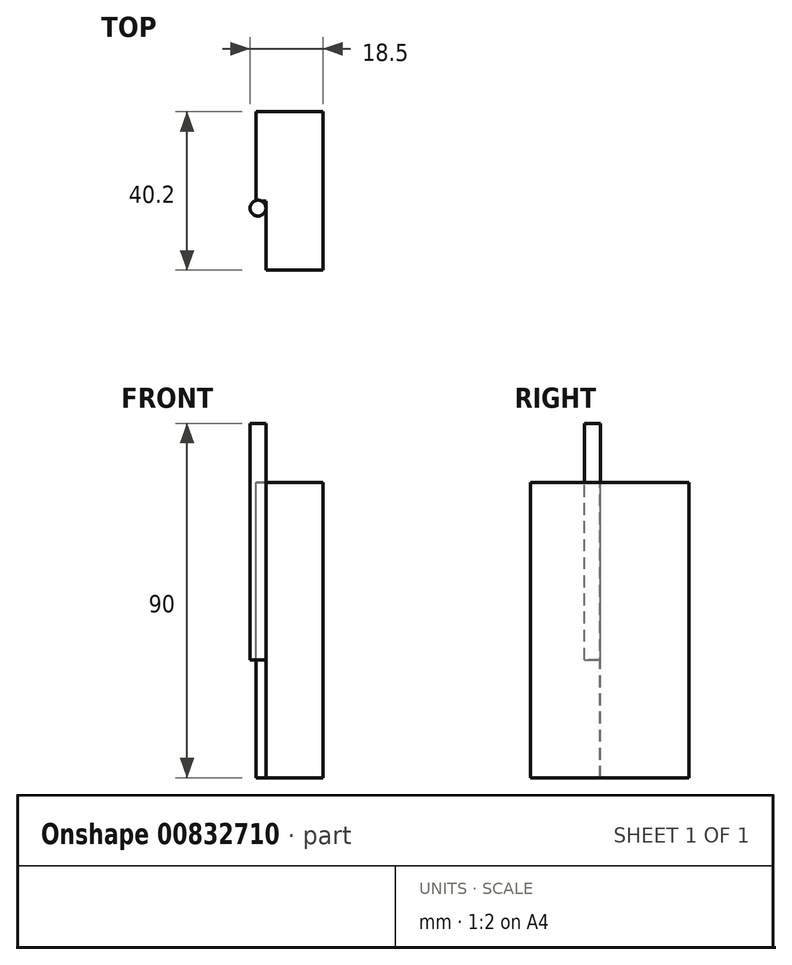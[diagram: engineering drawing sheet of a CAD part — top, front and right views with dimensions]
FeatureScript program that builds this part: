
annotation { "Feature Type Name" : "Feature", "Feature Type Description" : "" }
export const myFeature = defineFeature(function(context is Context, id is Id, definition is map)
    precondition{}
    {
        {
            var Q0;
            Q0=qCreatedBy(makeId("Top.planeOp"),FACE);
            var sketch = newSketch(context, id + "F0", { "sketchPlane" : qUnion([Q0])});
            skLineSegment(sketch, "E0", {"start": v(0, 0) * mm, "end": v(-14.5, 0) * mm});
            skLineSegment(sketch, "E1", {"start": v(-14.5, 0) * mm, "end": v(-14.5, 17.56) * mm});
            skLineSegment(sketch, "E2", {"start": v(-14.5, 17.56) * mm, "end": v(-17.04, 17.78) * mm});
            skLineSegment(sketch, "E3", {"start": v(-17.04, 17.78) * mm, "end": v(-17.04, 40.2) * mm});
            skCircle(sketch, "E4", {"center": v(-16.5, 15.73) * mm, "radius": 2 * mm});
            skLineSegment(sketch, "E5", {"start": v(-16.5, 15.73) * mm, "end": v(-18.5, 15.73) * mm, "construction": true});
            skLineSegment(sketch, "E6", {"start": v(-16.5, 15.73) * mm, "end": v(-16.5, 13.73) * mm, "construction": true});
            skLineSegment(sketch, "E7", {"start": v(-16.5, 13.73) * mm, "end": v(-30.83, 13.73) * mm, "construction": true});
            skPoint(sketch, "E8.orphan", {"position": v(0, 47.74) * mm});
            skLineSegment(sketch, "E9", {"start": v(-17.04, 40.2) * mm, "end": v(0, 40.2) * mm});
            skLineSegment(sketch, "E10.trimOffspring", {"start": v(0, 40.2) * mm, "end": v(0, 0) * mm});
            skSolve(sketch);
        }
        {
            var Q0;
            {var subQ6=sQuery(id+"F0.wireOp",EDGE,"E0");Q0=makeQuery(id+"F0.imprint","IMPRINT",FACE,{"disambiguationData":[TD([[makeQuery(id+"F0.imprint","IMPRINT",EDGE,{"derivedFrom":subQ6}),-1.0]])]});}
            extrude(context, id + "F1", {"entities" : qUnion([Q0]), "oppositeDirection" : true, "depth" : 75 * mm, "offsetDistance" : 25 * mm});
        }
        {
            var Q0;
            {var subQ0=sQuery(id+"F0.wireOp",EDGE,"E4");var subQ1=makeQuery(id+"F0.imprint","INTERSECT",VERTEX,{"derivedFrom":[sQuery(id+"F0.wireOp",EDGE,"E1"),subQ0]});Q0=makeQuery(id+"F0.imprint","IMPRINT",FACE,{"disambiguationData":[TD([[makeQuery(id+"F0.imprint","IMPRINT",EDGE,{"disambiguationData":[TD([[subQ1,-1.0]])],"derivedFrom":subQ0}),1.0]])]});}
            extrude(context, id + "F2", {"entities" : qUnion([Q0]), "operationType" : NewBodyOperationType.ADD, "oppositeDirection" : true, "depth" : 45 * mm, "offsetDistance" : 25 * mm, "hasSecondDirection" : true, "secondDirectionOppositeDirection" : false, "secondDirectionDepth" : 15 * mm});
        }
    });
